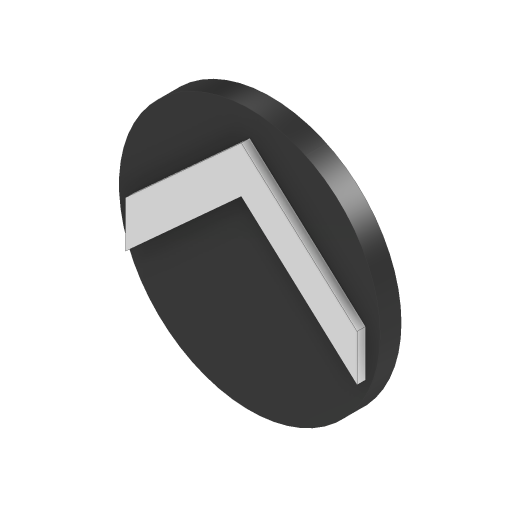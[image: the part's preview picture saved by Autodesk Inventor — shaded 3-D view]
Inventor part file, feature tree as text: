
AUTODESK INVENTOR PART (.ipt)
format: ipt  version: 2023 (Build 270158000, 158)  size: 247,808 bytes
history: native  units: mm
features: extrude x2, sketch x2, other x1
ambient origin geometry x8: Origin, YZ Plane, XZ Plane, XY Plane, X Axis, Y Axis, Z Axis, Center Point
bodies: Body1 (feature_tree)
feature tree (5):
  other  "Těleso1"
  extrude  "Vysunutí1"  Depth=12.4mm
  extrude  "Vysunutí2"  Depth=1.0mm TaperAngle=0.0deg
  sketch  "Náčrt1"
  sketch  "Náčrt2"
